# Revit family: Shower_Head-Whitehall-BestCare-WHCSH
name_source: partatom
category: Plumbing Fixtures
units: mm (PartAtom-declared; Revit-internal decimal feet)

## family parameters
Cut with Voids When Loaded = No
Host = Face
OmniClass Number = 23.45.05.14.17
OmniClass Title = Showers
Part Type = Normal
Room Calculation Point = No
Round Connector Dimension = Use Diameter
Shared = Yes

## types (3) — shared parameters
Assembly Code = D2020300
CW Connection = No
CWFU = 3
Default Elevation = 0"
Description = BestCare® Ligature-Resistant Conical Shower Head with Escutcheon
Escutcheon Material = Stainless Steel-Whitehall-Powder Coated
Finish = Brass-Whitehall-Chrome Plated
HW Connection = No
HWFU = 3
Height = 2 3/8"
Inlet Connection Diameter = 1/2"
Inlet Connection Radius = 1/4"
Installation Type = Wall Mounted
Length = 5 1/8"
Manufacturer = Whitehall Mfg.
Material = Brass-Whitehall-Chrome Plated
Product Documentation Link = https://www.whitehallmfg.com
Product Page URL = https://www.whitehallmfg.com
Tempered Water Connection = Yes
URL = https://www.whitehallmfg.com
Vent Connection = No
Waste Connection = No
Width = 5 1/8"
zero-valued in all types: WFU

## per-type parameters (varying)
| type | Flow Rate | Type Comments |
| WHCSH15 | 1.5 gallons (5.68 liters) per minute |  |
| WHCSH25 | 2.5 gallons (9.46 liters) per minute. |  |
| WHCSH15-WSB | 1.5 gallons (5.68 liters) per minute | WHCSH15-WSB showerhead has been certified by IAPMO per EPA WaterSense Criteria and has qualified for the official EPA WaterSense directory. |

note: column(s) folded — value = type name in every type: Model

## geometry (parser evidence)
native form markers: Sweep x3
no freeform markers — native parametric forms only
